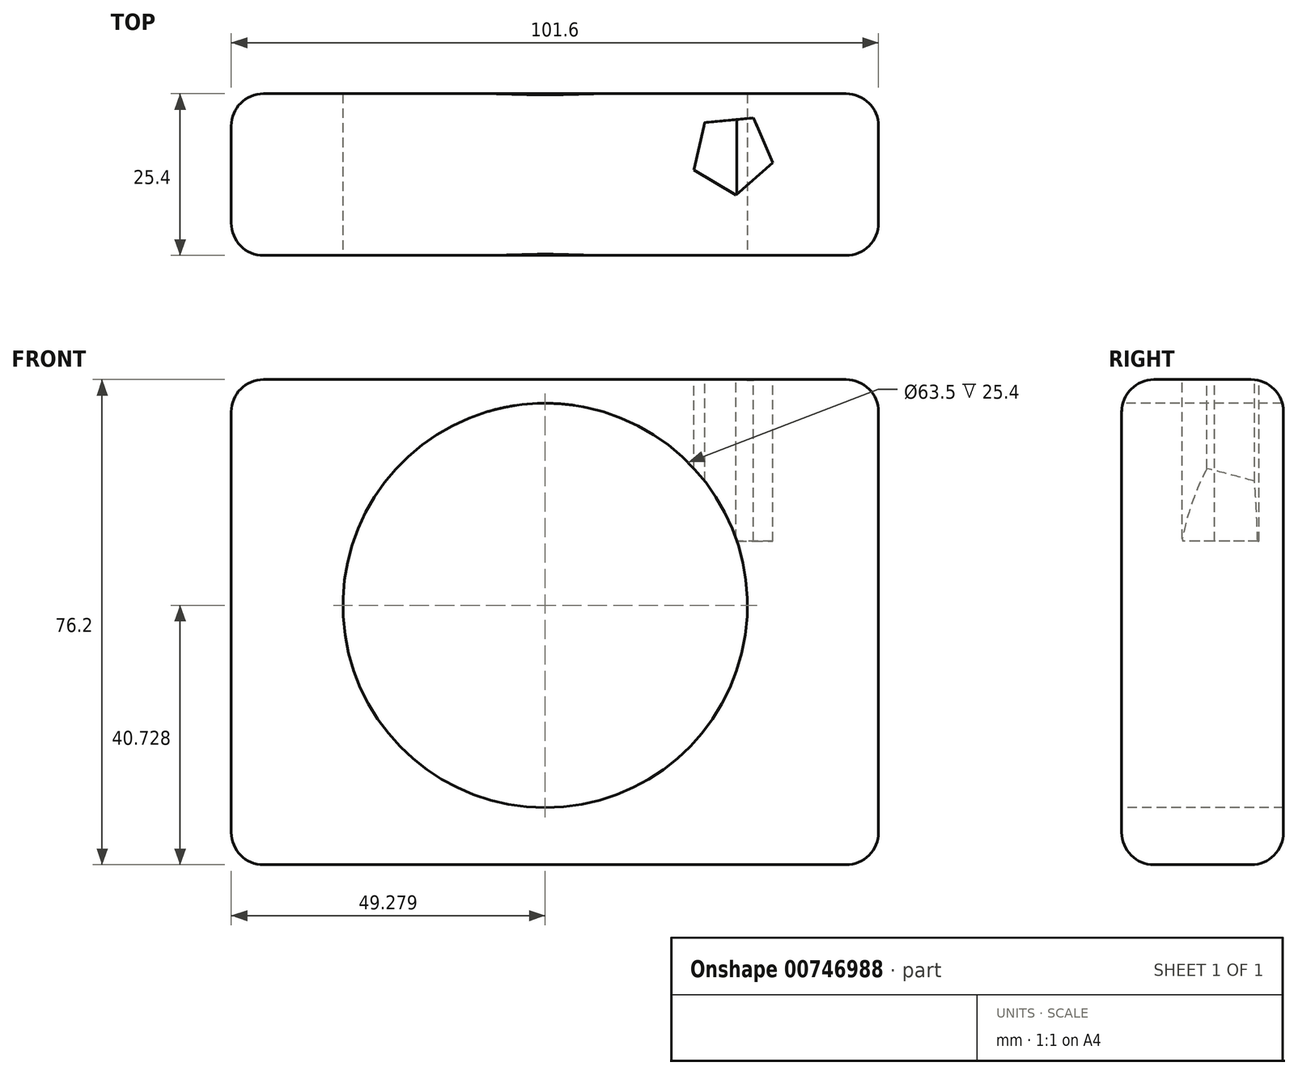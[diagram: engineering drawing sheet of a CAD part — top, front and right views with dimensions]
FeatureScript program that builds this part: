
annotation { "Feature Type Name" : "Feature", "Feature Type Description" : "" }
export const myFeature = defineFeature(function(context is Context, id is Id, definition is map)
    precondition{}
    {
        {
            var Q0;
            Q0=qCreatedBy(makeId("Front.planeOp"),FACE);
            var sketch = newSketch(context, id + "F0", { "sketchPlane" : qUnion([Q0])});
            skLineSegment(sketch, "E0.bottom", {"start": v(0, 0) * mm, "end": v(101.6, 0) * mm});
            skLineSegment(sketch, "E0.top", {"start": v(0, 76.2) * mm, "end": v(101.6, 76.2) * mm});
            skLineSegment(sketch, "E0.left", {"start": v(0, 0) * mm, "end": v(0, 76.2) * mm});
            skLineSegment(sketch, "E0.right", {"start": v(101.6, 0) * mm, "end": v(101.6, 76.2) * mm});
            skSolve(sketch);
        }
        {
            var Q0;
            Q0=makeQuery(id+"F0.imprint","IMPRINT",FACE,{"disambiguationData":[TD([[makeQuery(id+"F0.imprint","IMPRINT",EDGE,{"derivedFrom":sQuery(id+"F0.wireOp",EDGE,"E0.bottom")}),1.0]])]});
            extrude(context, id + "F1", {"entities" : qUnion([Q0]), "depth" : 25.4 * mm, "offsetDistance" : 25.4 * mm});
        }
        {
            var Q0;
            Q0=makeQuery(id+"F1.opExtrude","SWEPT_FACE",FACE,{"disambiguationData":[OSD([sQuery(id+"F0.wireOp",EDGE,"E0.top")])]});
            var Q1;
            Q1=makeQuery(id+"F1.opExtrude","CAP_FACE",FACE,{"disambiguationData":[OSD([sQuery(id+"F0.wireOp",EDGE,"E0.bottom"),sQuery(id+"F0.wireOp",EDGE,"E0.top"),sQuery(id+"F0.wireOp",EDGE,"E0.left"),sQuery(id+"F0.wireOp",EDGE,"E0.right")])],"isStart":false});
            var Q2;
            Q2=makeQuery(id+"F1.opExtrude","SWEPT_FACE",FACE,{"disambiguationData":[OSD([sQuery(id+"F0.wireOp",EDGE,"E0.left")])]});
            var Q3;
            Q3=makeQuery(id+"F1.opExtrude","SWEPT_FACE",FACE,{"disambiguationData":[OSD([sQuery(id+"F0.wireOp",EDGE,"E0.right")])]});
            var Q4;
            Q4=makeQuery(id+"F1.opExtrude","CAP_FACE",FACE,{"disambiguationData":[OSD([sQuery(id+"F0.wireOp",EDGE,"E0.bottom"),sQuery(id+"F0.wireOp",EDGE,"E0.top"),sQuery(id+"F0.wireOp",EDGE,"E0.left"),sQuery(id+"F0.wireOp",EDGE,"E0.right")])],"isStart":true});
            var Q5;
            Q5=makeQuery(id+"F1.opExtrude","SWEPT_FACE",FACE,{"disambiguationData":[OSD([sQuery(id+"F0.wireOp",EDGE,"E0.bottom")])]});
            fillet(context, id + "F2", {"entities" : qUnion([Q0, Q1, Q2, Q3, Q4, Q5]), "radius" : 5.08 * mm, "tangentPropagation" : true, "allowEdgeOverflow" : false});
        }
        {
            var Q0;
            Q0=makeQuery(id+"F1.opExtrude","CAP_FACE",FACE,{"disambiguationData":[OSD([sQuery(id+"F0.wireOp",EDGE,"E0.bottom"),sQuery(id+"F0.wireOp",EDGE,"E0.top"),sQuery(id+"F0.wireOp",EDGE,"E0.left"),sQuery(id+"F0.wireOp",EDGE,"E0.right")])],"isStart":false});
            var sketch = newSketch(context, id + "F3", { "sketchPlane" : qUnion([Q0])});
            skCircle(sketch, "E1", {"center": v(49.28, 40.73) * mm, "radius": 31.75 * mm});
            skSolve(sketch);
        }
        {
            var Q0;
            Q0 = qSketchRegion(id + "F3", true);
            extrude(context, id + "F4", {"entities" : qUnion([Q0]), "operationType" : NewBodyOperationType.REMOVE, "oppositeDirection" : true, "depth" : 25.4 * mm, "offsetDistance" : 25.4 * mm});
        }
        {
            var Q0;
            Q0=makeQuery(id+"F1.opExtrude","SWEPT_FACE",FACE,{"disambiguationData":[OSD([sQuery(id+"F0.wireOp",EDGE,"E0.top")])]});
            var sketch = newSketch(context, id + "F5", { "sketchPlane" : qUnion([Q0])});
            skCircle(sketch, "E2.cCircle", {"center": v(78.64, -9.42) * mm, "radius": 5.27 * mm, "construction": true});
            skLineSegment(sketch, "E2.0", {"start": v(85, -10.84) * mm, "end": v(79.25, -15.9) * mm});
            skLineSegment(sketch, "E2.1", {"start": v(79.25, -15.9) * mm, "end": v(72.66, -12.01) * mm});
            skLineSegment(sketch, "E2.2", {"start": v(72.66, -12.01) * mm, "end": v(74.33, -4.53) * mm});
            skLineSegment(sketch, "E2.3", {"start": v(74.33, -4.53) * mm, "end": v(81.95, -3.8) * mm});
            skLineSegment(sketch, "E2.4", {"start": v(81.95, -3.8) * mm, "end": v(85, -10.84) * mm});
            skPoint(sketch, "E2.0.midPoint", {"position": v(82.13, -13.37) * mm});
            skSolve(sketch);
        }
        {
            var Q0;
            Q0 = qSketchRegion(id + "F5", true);
            extrude(context, id + "F6", {"entities" : qUnion([Q0]), "operationType" : NewBodyOperationType.REMOVE, "oppositeDirection" : true, "depth" : 25.4 * mm, "offsetDistance" : 25.4 * mm});
        }
    });
